# Revit family: Connection-Cleat Plate-Steel & Tube-HST General Purpose
name_source: partatom
category: Structural Connections
revit_build: Autodesk Revit 2018 (Build: 20170927_1515(x64)
units: mm (PartAtom-declared; Revit-internal decimal feet)

## family parameters
Cut with Voids When Loaded = No
Enable cutting in views = Yes
Host = Face
Material for Model Behavior = Steel
OmniClass Number = 23.25.05.17.11
OmniClass Title = Column Bases
Shared = Yes

## types (6) — shared parameters
Assembly Code = B1020230
CBICode = 3411
CBIDescription = Structural steelwork
Description = HST Steel Purlins and Girts are high strength lipped profile sections, providing an economic solution for your building project.
Design Instruction = All the design information should be cross referenced with the current Steel & Tube Purlins and Girts design guide, and AS/NZS 4600:2005
Design Standard = Steel & Tube’s HST purlins and Girts profiles are designed in accordance with AS/NZS 4600:2005.
Length_ANZRS = 70 mm  [stored 0.229659 ft]
Manufacturer = Steel & Tube
ManufacturerName = Steel & Tube
ManufacturerURL = http://www.steelandtube.co.nz
Material Standard = Steel & Tube’s HST purlins and Girts profiles are manufactured from materials conforming to AS1397:2011
Material_ANZRS = Metal-Steel-450MPa
ModifiedIssue_ANZRS = 20160520 $
PlateThickness_ANZRS = 2 mm  [stored 0.00656168 ft]
SpecificationDescription = Steel & Tube Purlins & Girts
SpecificationReference = 3411ST
Type Comments = HST Steel Purlin General Purpose Cleat - Non Structural Only
URL = http://www.steelandtube.co.nz
Uniclass2015Code = Pr_20_76_51_21
Uniclass2015Title = Cold-formed galvanized steel sections
Uniclass2015Version = 2015
zero-valued in all types: Default Elevation

## per-type parameters (varying)
| type | Beam Size | Height_ANZRS | Width_ANZRS | b | d |
| HST150 | 152 mm | 130 mm | 112 mm | 80 mm | 65 mm  [stored 0.213255 ft] |
| HST200 | 203 mm | 130 mm | 155 mm | 120 mm | 75 mm |
| HST250 | 250 mm | 150 mm | 195 mm | 160 mm | 85 mm |
| HST300 | 300 mm | 150 mm | 235 mm | 200 mm | 95 mm |
| HST350 | 350 mm | 180 mm | 290 mm | 240 mm | 105 mm |
| HST400 | 400 mm | 180 mm | 330 mm | 280 mm | 115 mm |

note: column(s) folded — value = type name in every type: Model

note: [stored X ft] marks values corroborated as IEEE doubles in the binary element streams (Revit-internal decimal feet)

## geometry (parser evidence)
native form markers: Sweep x2
no freeform markers — native parametric forms only
